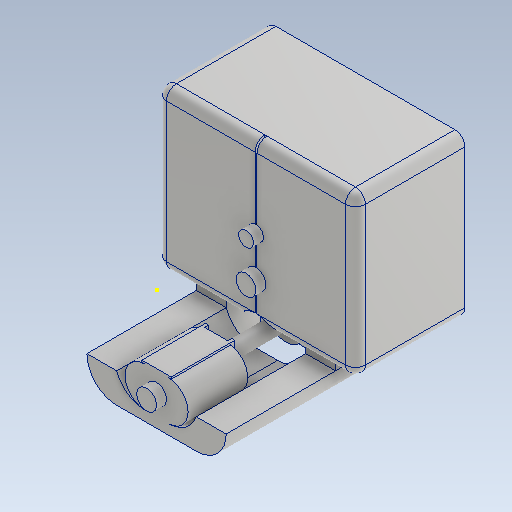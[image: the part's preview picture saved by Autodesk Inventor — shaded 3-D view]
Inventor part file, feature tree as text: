
AUTODESK INVENTOR PART (.ipt)
format: ipt  version: 2021 (Build 250183000, 183)  size: 436,224 bytes
history: native  units: mm
features: sketch x27, extrude x25, fillet x5, plane x2
ambient origin geometry x8: Origin, YZ Plane, XZ Plane, XY Plane, X Axis, Y Axis, Z Axis, Center Point
bodies: Solid1 (feature_tree)
feature tree (59):
  extrude  "Extrusion1"  Depth=80.0mm
  extrude  "Extrusion2"  Depth=50.0mm
  sketch  "Sketch3"  dims[d4=50.0mm d5=0.0mm d6=80.0mm]
  sketch  "Sketch4"  dims[d7=20.0mm d8=0.0mm d9=70.0mm]
  extrude  "Extrusion3"  Depth=50.0mm
  extrude  "Extrusion4"  Depth=70.0mm
  extrude  "Extrusion5"  Depth=20.0mm TaperAngle=0.0deg
  fillet  "Fillet1"  Radius=15.0mm
  sketch  "Sketch7"  dims[d20=40.0mm d21=55.0mm d22=0.0mm]
  extrude  "Extrusion6"  Depth=5.0mm TaperAngle=0.0deg
  fillet  "Fillet2"  Radius=15.0mm
  fillet  "Fillet3"  Radius=10.0mm
  extrude  "Extrusion7"  Depth=55.0mm TaperAngle=0.0deg
  extrude  "Extrusion8"  Depth=15.0mm
  extrude  "Extrusion9"  Depth=90.0mm
  extrude  "Extrusion10"  Depth=45.0mm TaperAngle=0.0deg
  extrude  "Extrusion12"  Depth=5.0mm TaperAngle=0.0deg
  extrude  "Extrusion13"  Depth=5.0mm TaperAngle=0.0deg
  extrude  "Extrusion14"  Depth=21.0mm
  extrude  "Extrusion15"  Depth=2.0mm TaperAngle=0.0deg
  extrude  "Extrusion16"  Depth=1.0mm TaperAngle=0.0deg
  extrude  "Extrusion17"  Depth=10.0mm
  fillet  "Fillet4"  Radius=4.0mm
  plane  "Work Plane1"
  extrude  "Extrusion21"  Depth=10.0mm
  extrude  "Extrusion22"  Depth=5.0mm
  plane  "Work Plane2"
  extrude  "Extrusion23"  Depth=50.0mm TaperAngle=0.0deg
  extrude  "Extrusion24"  TaperAngle=0.0deg  [1 undecoded]
  extrude  "Extrusion25"  Depth=5.0mm
  extrude  "Extrusion26"  Depth=20.0mm
  extrude  "Extrusion27"  Depth=5.0mm TaperAngle=0.0deg
  extrude  "Extrusion28"  Depth=5.0mm TaperAngle=0.0deg
  extrude  "Extrusion29"  Depth=49.75mm
  fillet  "Fillet5"  Radius=7.5mm
  sketch  "Sketch1"  dims[d0=100.0mm d1=80.0mm]
  sketch  "Sketch2"  dims[d2=40.0mm d3=50.0mm]
  sketch  "Sketch5"  dims[d10=15.0mm d11=20.0mm d12=0.0mm d13=15.0mm]
  sketch  "Sketch6"  dims[d14=20.0mm d15=0.0mm d16=5.0mm d17=0.0mm d18=15.0mm d19=10.0mm]
  sketch  "Sketch8"  dims[d23=15.0mm d24=15.0mm]
  sketch  "Sketch9"  dims[d25=30.0mm d26=0.0mm d27=90.0mm]
  sketch  "Sketch10"  dims[d28=70.0mm d29=45.0mm d30=0.0mm]
  sketch  "Sketch11"  dims[d31=10.0mm d32=5.0mm d33=0.0mm]
  sketch  "Sketch12"  dims[d34=7.5mm d35=5.0mm d36=0.0mm]
  sketch  "Sketch14"  dims[d40=1.5mm d41=21.0mm]
  sketch  "Sketch15"  dims[d42=1.5mm d43=2.0mm d44=0.0mm]
  sketch  "Sketch16"  dims[d45=1.5mm d46=1.0mm d47=0.0mm]
  sketch  "Sketch17"  dims[d48=1.0mm d49=0.0mm d50=10.0mm d51=4.0mm d52=0.0mm]
  sketch  "Sketch18"  dims[d53=10.0mm d54=0.0mm d55=7.5mm]
  sketch  "Sketch19"  dims[d56=5.0mm d57=0.0mm d58=5.0mm]
  sketch  "Sketch24"  dims[d59=0.0mm d64=50.0mm d75=17.5mm d76=0.0mm]
  sketch  "Sketch25"  dims[d77=20.0mm d78=0.0mm d79=0.0mm]
  sketch  "Sketch26"  dims[d80=20.0mm d81=0.0mm d85=66.0mm d92=5.0mm]
  sketch  "Sketch29"  dims[d97=40.0mm d98=20.0mm]
  sketch  "Sketch30"  dims[d99=5.0mm d100=0.0mm d101=5.0mm d102=0.0mm]
  sketch  "Sketch31"  dims[d103=40.0mm d105=5.0mm d106=0.0mm]
  sketch  "Sketch32"  dims[d107=49.75mm d108=49.75mm d109=7.5mm]
  sketch  "Sketch33"  dims[d110=20.0mm]
  sketch  "Sketch34"  dims[d111=49.5mm d112=49.5mm d113=5.0mm d114=0.0mm d115=7.5mm d116=10.0mm d117=5.0mm d118=0.0mm d119=10.0mm d120=7.5mm d121=5.0mm d122=0.0mm d123=5.0mm]
note: 1 required parameter value undecoded (feature->parameter linkage not recoverable at this tier; creation-order binding heuristic only, values carry confidence <= 0.55)
